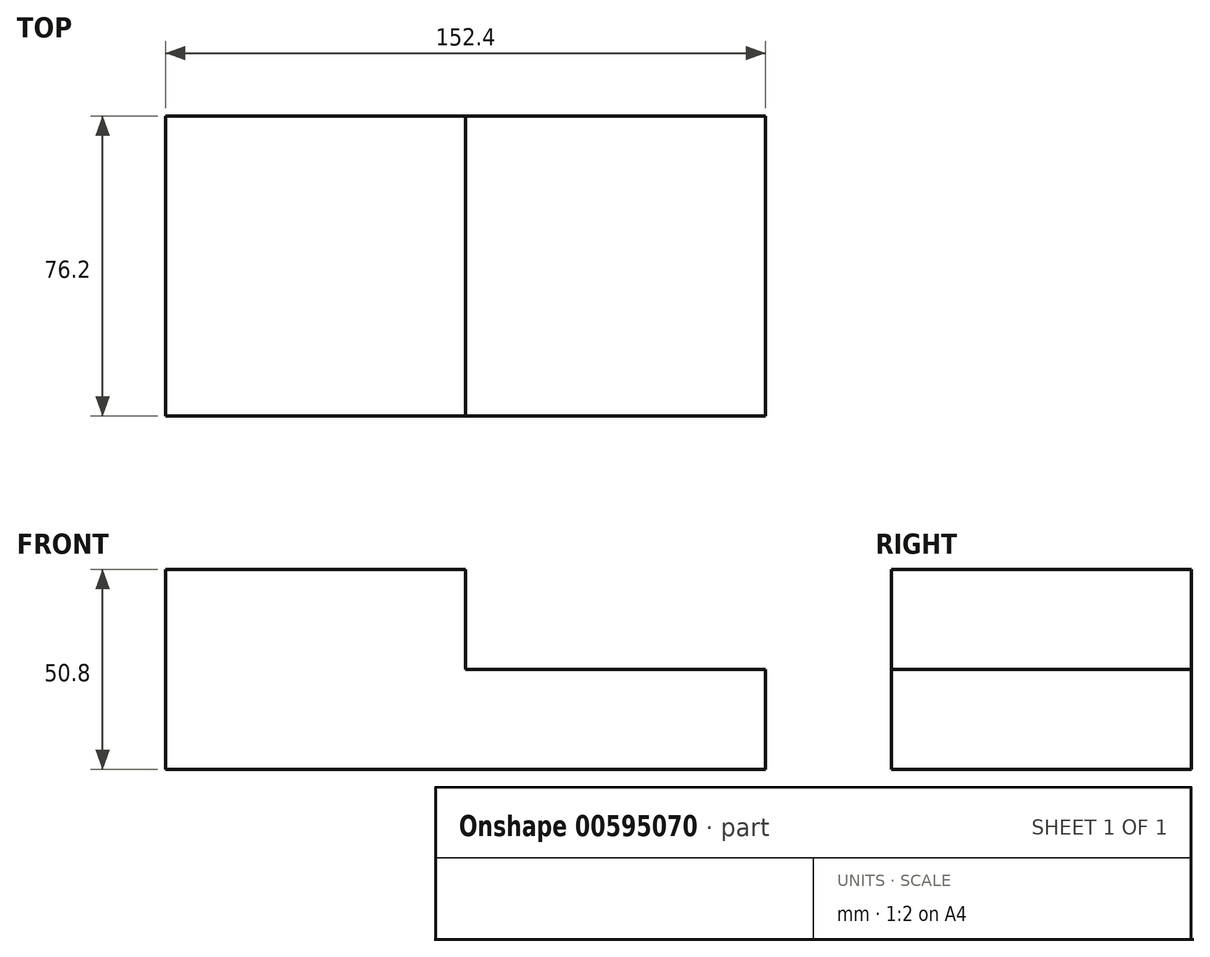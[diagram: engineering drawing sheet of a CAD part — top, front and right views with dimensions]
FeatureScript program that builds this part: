
annotation { "Feature Type Name" : "Feature", "Feature Type Description" : "" }
export const myFeature = defineFeature(function(context is Context, id is Id, definition is map)
    precondition{}
    {
        {
            var Q0;
            Q0=qCreatedBy(makeId("Front.planeOp"),FACE);
            var sketch = newSketch(context, id + "F0", { "sketchPlane" : qUnion([Q0])});
            skLineSegment(sketch, "E0", {"start": v(0, 0) * mm, "end": v(0, 50.8) * mm});
            skLineSegment(sketch, "E1", {"start": v(0, 50.8) * mm, "end": v(76.2, 50.8) * mm});
            skLineSegment(sketch, "E2", {"start": v(76.2, 50.8) * mm, "end": v(76.2, 25.4) * mm});
            skLineSegment(sketch, "E3", {"start": v(76.2, 25.4) * mm, "end": v(152.4, 25.4) * mm});
            skLineSegment(sketch, "E4", {"start": v(152.4, 25.4) * mm, "end": v(152.4, 0) * mm});
            skLineSegment(sketch, "E5", {"start": v(152.4, 0) * mm, "end": v(0, 0) * mm});
            skSolve(sketch);
        }
        {
            var Q0;
            Q0 = qSketchRegion(id + "F0", true);
            extrude(context, id + "F1", {"entities" : qUnion([Q0]), "depth" : 76.2 * mm, "offsetDistance" : 25.4 * mm});
        }
    });
